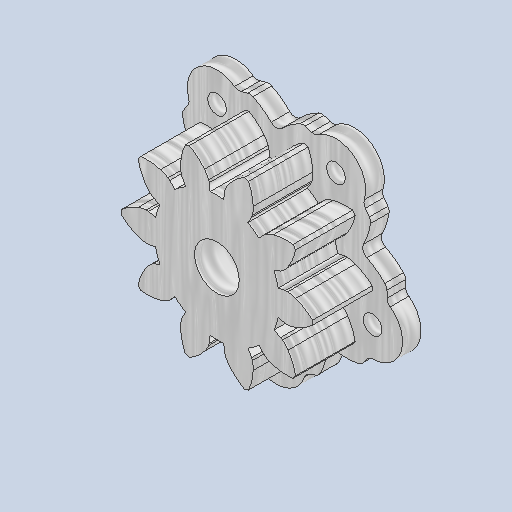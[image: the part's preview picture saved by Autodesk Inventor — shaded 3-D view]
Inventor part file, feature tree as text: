
AUTODESK INVENTOR PART (.ipt)
format: ipt  version: 2023 (Build 270158030, 158C)  size: 729,088 bytes
history: native  units: mm
features: sketch x3, extrude x2, projected_geometry x2, fillet x1
ambient origin geometry x8: Origin, YZ Plane, XZ Plane, XY Plane, X Axis, Y Axis, Z Axis, Center Point
bodies: Body1 (feature_tree)
feature tree (8):
  extrude  "押し出し2"  Depth=6.0mm
  extrude  "押し出し3"  Depth=8.0mm TaperAngle=0.0deg
  fillet  "フィレット1"  Radius=2.5mm
  sketch  "スケッチ5"
  sketch  "スケッチ3"
  sketch  "スケッチ4"
  projected_geometry  "投影ループ1"
  projected_geometry  "投影ループ2"
